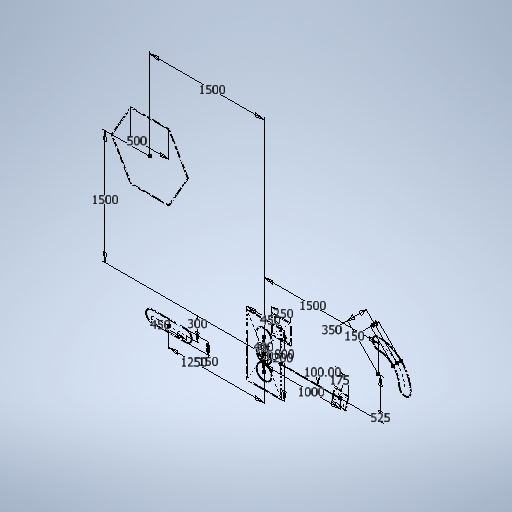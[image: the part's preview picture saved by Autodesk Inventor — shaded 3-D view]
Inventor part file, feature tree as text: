
AUTODESK INVENTOR PART (.ipt)
format: ipt  version: 2025.2 (Build 292293000, 293)  size: 292,864 bytes
history: native  units: in
note: dims shown in document units (in); Inventor stores cm internally (conversion verified against a paired STEP export)
features: sketch x1
ambient origin geometry x8: Origin, YZ Plane, XZ Plane, XY Plane, X Axis, Y Axis, Z Axis, Center Point
feature tree (1):
  sketch  "Sketch1"  dims[d0=15.748in d1=7.874in d2=1.9685in d3=2.9528in d4=17.7165in d5=31.4961in d6=9.8425in d7=39.3701in d8=0.6871in d9=6.8898in d10=17.7165in d11=11.811in d12=49.2126in d13=5.9055in d15=5.9055in d16=13.7795in d17=59.0551in d18=20.6693in d19=59.0551in d20=59.0551in d21=19.685in]
